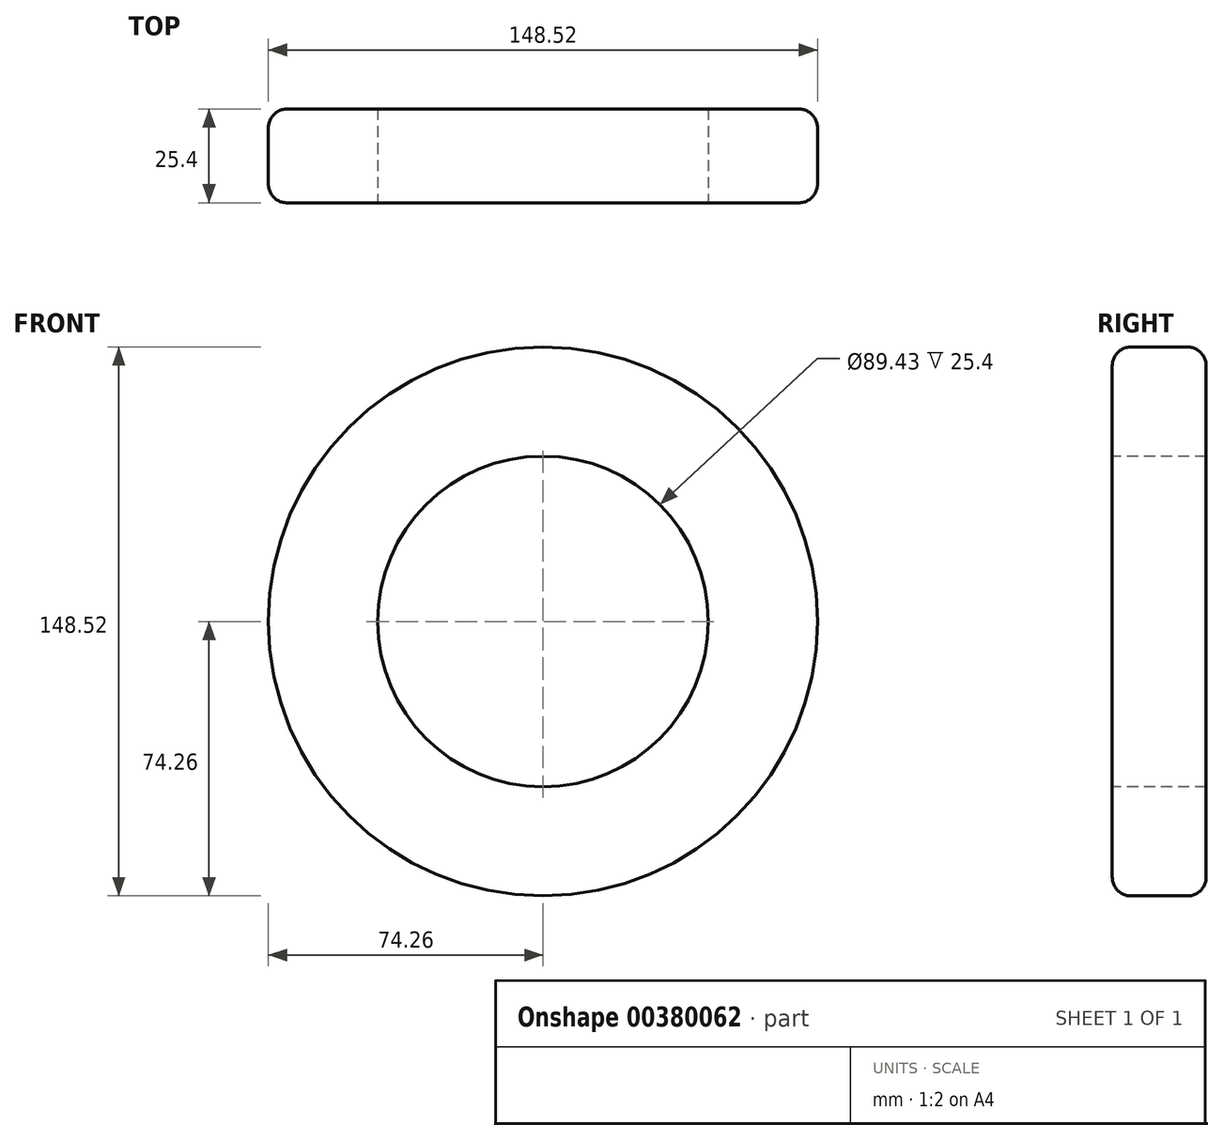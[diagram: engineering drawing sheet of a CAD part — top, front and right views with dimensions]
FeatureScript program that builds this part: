
annotation { "Feature Type Name" : "Feature", "Feature Type Description" : "" }
export const myFeature = defineFeature(function(context is Context, id is Id, definition is map)
    precondition{}
    {
        {
            var Q0;
            Q0=qCreatedBy(makeId("Front.planeOp"),FACE);
            var sketch = newSketch(context, id + "F0", { "sketchPlane" : qUnion([Q0])});
            skCircle(sketch, "E0", {"center": v(0, 0) * mm, "radius": 74.26 * mm});
            skSolve(sketch);
        }
        {
            var Q0;
            Q0 = qSketchRegion(id + "F0", true);
            extrude(context, id + "F1", {"entities" : qUnion([Q0]), "depth" : 25.4 * mm});
        }
        {
            var Q0;
            Q0=makeQuery(id+"F1.opExtrude","CAP_FACE",FACE,{"disambiguationData":[OSD([sQuery(id+"F0.wireOp",EDGE,"E0")])],"isStart":false});
            var sketch = newSketch(context, id + "F2", { "sketchPlane" : qUnion([Q0])});
            skCircle(sketch, "E1", {"center": v(0, 0) * mm, "radius": 44.71 * mm});
            skSolve(sketch);
        }
        {
            var Q0;
            Q0 = qSketchRegion(id + "F2", true);
            extrude(context, id + "F3", {"entities" : qUnion([Q0]), "operationType" : NewBodyOperationType.REMOVE, "oppositeDirection" : true, "depth" : 25.4 * mm});
        }
        {
            var Q0;
            Q0=makeQuery(id+"F1.opExtrude","CAP_EDGE",EDGE,{"disambiguationData":[OSD([sQuery(id+"F0.wireOp",EDGE,"E0")])],"isStart":false});
            var Q1;
            Q1=makeQuery(id+"F1.opExtrude","CAP_EDGE",EDGE,{"disambiguationData":[OSD([sQuery(id+"F0.wireOp",EDGE,"E0")])],"isStart":true});
            fillet(context, id + "F4", {"entities" : qUnion([Q0, Q1]), "radius" : 5.08 * mm, "tangentPropagation" : true, "allowEdgeOverflow" : false});
        }
    });
